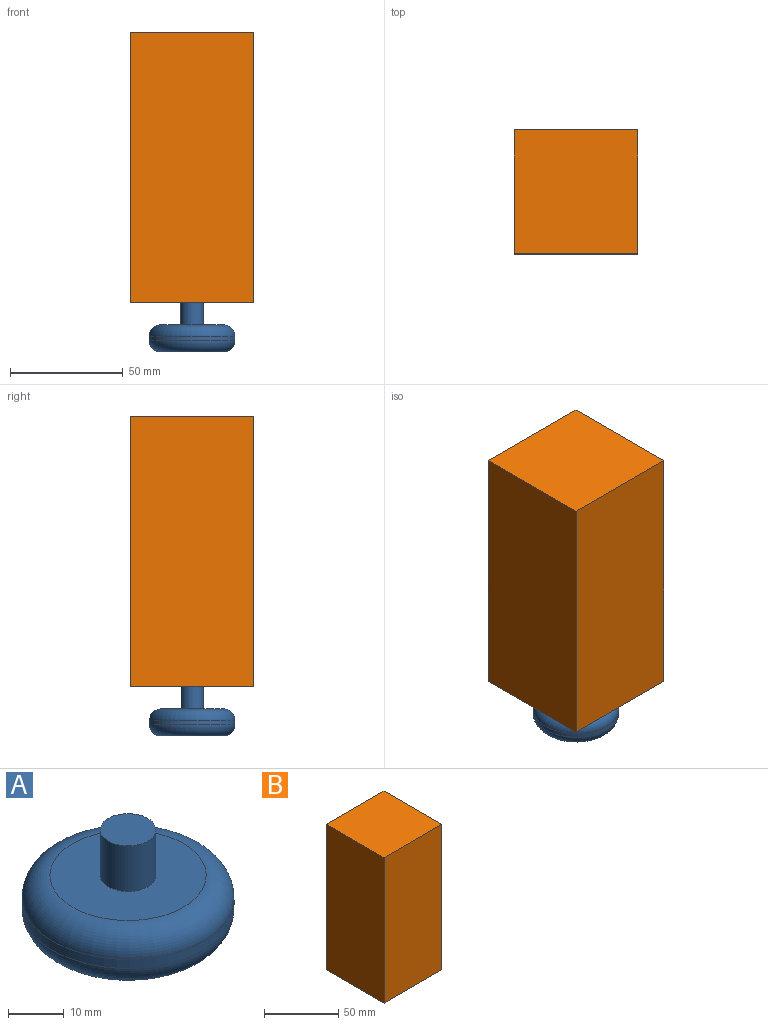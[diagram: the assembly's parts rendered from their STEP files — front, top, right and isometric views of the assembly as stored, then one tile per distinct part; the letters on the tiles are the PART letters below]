
ASSEMBLY  parts=2 mates=1
PART A: 7 faces, bbox 41.1x41.1x22 mm
  f0: cylinder r=19mm len=38mm, axis (0,0,-1), area 238.8mm2, adj f3,f4
  f1: plane 28x28mm, normal (0,0,1), area 537.2mm2, adj f4,f5
  f2: plane 28x28mm, normal (0,0,-1), area 615.8mm2, adj f3
  f3: torus R=14mm, axis (0,0,1), area 848mm2, adj f0,f2
  f4: torus R=14mm, axis (0,0,1), area 848mm2, adj f0,f1
  f5: cylinder r=5mm len=10mm, axis (0,0,-1), area 314.2mm2, adj f1,f6
  f6: plane 10x10mm, normal (0,0,1), area 78.5mm2, adj f5
PART B: 6 faces, bbox 55x55x120 mm
  f0: plane 120x55mm, normal (0,1,0), area 6600mm2, adj f1,f3,f4,f5
  f1: plane 120x55mm, normal (-1,0,0), area 6600mm2, adj f0,f2,f4,f5
  f2: plane 120x55mm, normal (0,-1,0), area 6600mm2, adj f1,f3,f4,f5
  f3: plane 120x55mm, normal (1,0,0), area 6600mm2, adj f0,f2,f4,f5
  f4: plane 55x55mm, normal (0,0,1), area 3025mm2, adj f0,f1,f2,f3
  f5: plane 55x55mm, normal (0,0,-1), area 3025mm2, adj f0,f1,f2,f3
PLACE A rot(axis=(0,0,-1),90deg) t=(-34.61,60.94,0)mm
PLACE B rot(axis=(0.71,-0.71,0),180deg) t=(17.73,46.07,142)mm fixed
MATE fastened B.f4 <-> A.f0  axis (0,0,-1) through (13.16,47.77,22)mm
